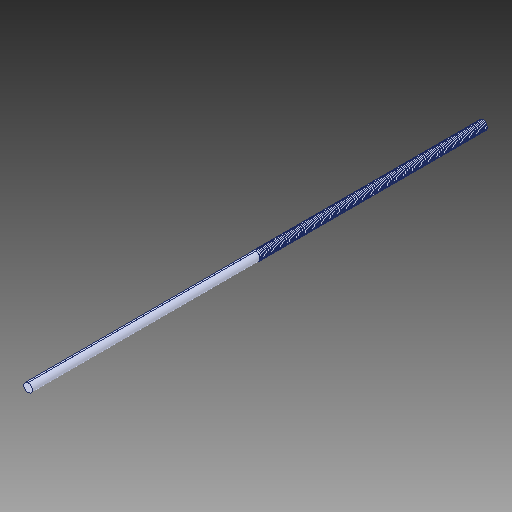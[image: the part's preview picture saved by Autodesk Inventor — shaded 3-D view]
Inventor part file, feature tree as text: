
AUTODESK INVENTOR PART (.ipt)
format: ipt  version: 2019 (Build 230136000, 136)  size: 2,197,504 bytes
history: native  units: in
note: dims shown in document units (in); Inventor stores cm internally (conversion verified against a paired STEP export)
features: other x3, sketch x1
ambient origin geometry x8: Origin, YZ Plane, XZ Plane, XY Plane, X Axis, Y Axis, Z Axis, Center Point
bodies: Solid1 (feature_tree)
feature tree (4):
  other  "LeadScrew.ipt"
  other  "Solid1::LeadScrew.ipt"
  other  "TaggingFeature1"
  sketch  "Sketch1"  dims[d0=0.3937in]
